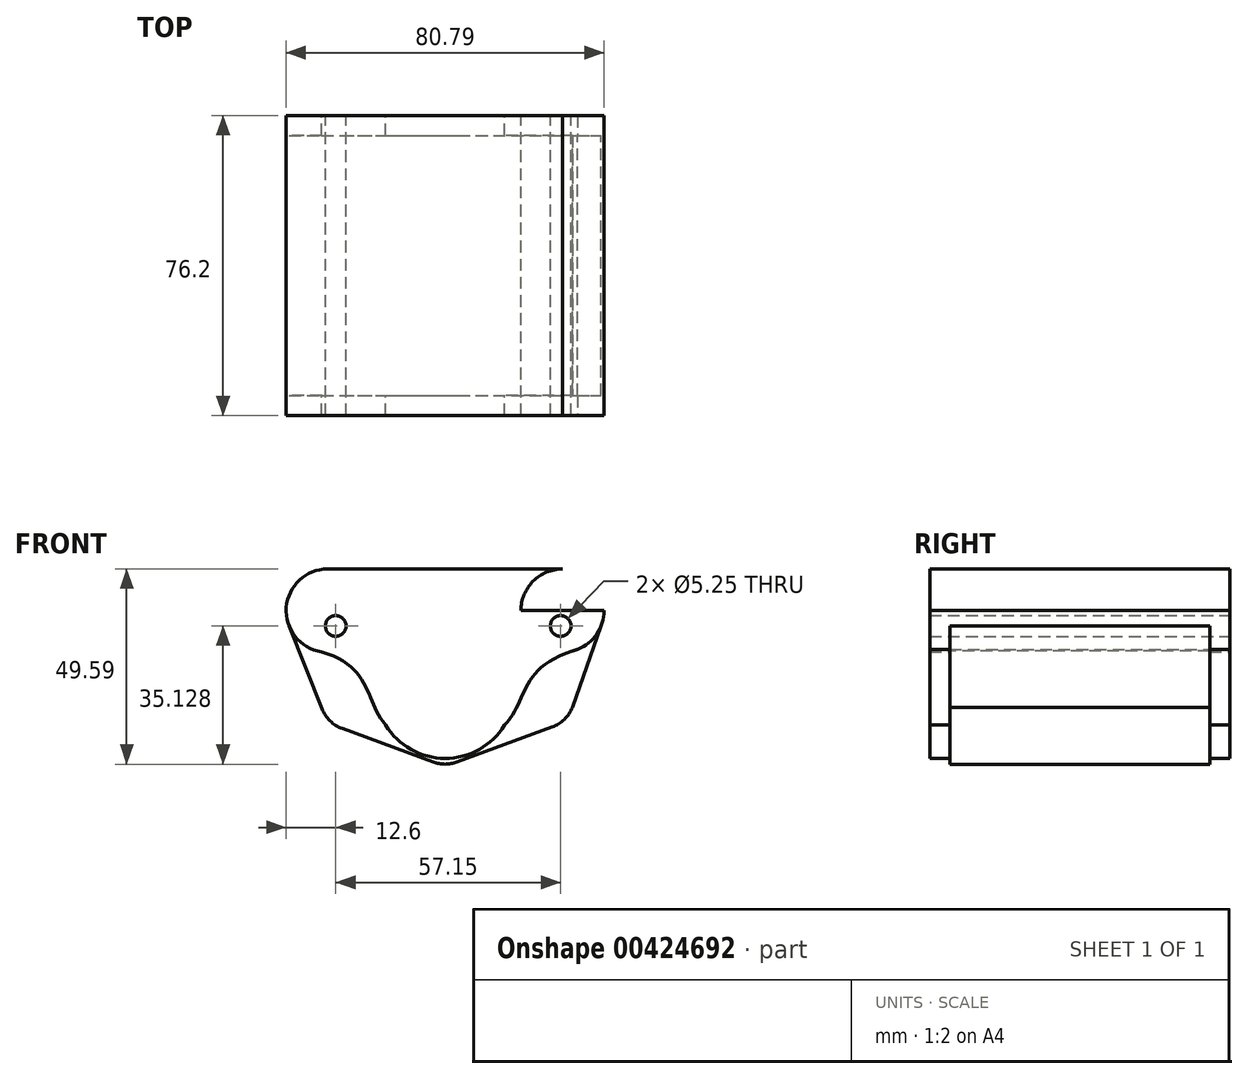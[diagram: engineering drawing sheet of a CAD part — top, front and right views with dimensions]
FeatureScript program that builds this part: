
annotation { "Feature Type Name" : "Feature", "Feature Type Description" : "" }
export const myFeature = defineFeature(function(context is Context, id is Id, definition is map)
    precondition{}
    {
        {
            var Q0;
            Q0=qCreatedBy(makeId("Front.planeOp"),FACE);
            var sketch = newSketch(context, id + "F0", { "sketchPlane" : qUnion([Q0])});
            skLineSegment(sketch, "E0", {"start": v(-40.39, -0.14) * mm, "end": v(40.39, -0.14) * mm});
            skLineSegment(sketch, "E1", {"start": v(0, 11.4) * mm, "end": v(0, -39.74) * mm});
            skCircle(sketch, "E2", {"center": v(0, -20) * mm, "radius": 14.52 * mm});
            skCircle(sketch, "E3", {"center": v(29.82, -0.13) * mm, "radius": 10.56 * mm});
            skCircle(sketch, "E4", {"center": v(-29.83, -0.14) * mm, "radius": 10.56 * mm});
            skLineSegment(sketch, "E5", {"start": v(-29.83, 10.43) * mm, "end": v(29.82, 10.43) * mm});
            skCircle(sketch, "E6", {"center": v(0, -20) * mm, "radius": 17.68 * mm});
            skLineSegment(sketch, "E7", {"start": v(-26.1, -30.13) * mm, "end": v(-3.07, -38.6) * mm});
            skLineSegment(sketch, "E8", {"start": v(3.07, -38.6) * mm, "end": v(27.16, -29.73) * mm});
            skLineSegment(sketch, "E9", {"start": v(32.35, -24.67) * mm, "end": v(39.64, -4.03) * mm});
            skLineSegment(sketch, "E10", {"start": v(-31.3, -25.07) * mm, "end": v(-39.65, -4.04) * mm});
            skArc(sketch, "E11.filletArc", {"start": v(27.16, -29.73) * mm, "mid": v(30.3, -27.76) * mm, "end": v(32.35, -24.67) * mm});
            skPoint(sketch, "E12.visualSharp", {"position": v(-29.83, -28.75) * mm});
            skArc(sketch, "E12.filletArc", {"start": v(-31.3, -25.07) * mm, "mid": v(-29.24, -28.15) * mm, "end": v(-26.1, -30.13) * mm});
            skPoint(sketch, "E13.visualSharp", {"position": v(0, -39.74) * mm});
            skArc(sketch, "E13.filletArc", {"start": v(-3.07, -38.6) * mm, "mid": v(0, -39.16) * mm, "end": v(3.07, -38.6) * mm});
            skPoint(sketch, "E14.1.internal.snap0", {"position": v(15.12, -34.17) * mm});
            skFitSpline(sketch, "E14", {"points": [v(33.66, -9.98) * mm, v(15.12, -29.17) * mm], "startDerivative": vector(-45.98, -13.6) * mm, "endDerivative": vector(-18.55, -19.19) * mm});
            skFitSpline(sketch, "E15", {"points": [v(-31.45, -10.58) * mm, v(-15.12, -29.17) * mm], "startDerivative": vector(39.1, -11.38) * mm, "endDerivative": vector(16.33, -18.6) * mm});
            skCircle(sketch, "E16", {"center": v(29.35, -4.03) * mm, "radius": 2.63 * mm});
            skCircle(sketch, "E17", {"center": v(-27.8, -4.03) * mm, "radius": 2.63 * mm});
            skSolve(sketch);
        }
        {
            var Q0;
            {var subQ0=sQuery(id+"F0.wireOp",EDGE,"E7");Q0=makeQuery(id+"F0.imprint","IMPRINT",FACE,{"disambiguationData":[TD([[makeQuery(id+"F0.imprint","IMPRINT",EDGE,{"derivedFrom":subQ0}),1.0]])]});}
            var Q1;
            {var subQ11=sQuery(id+"F0.wireOp",EDGE,"E8");Q1=makeQuery(id+"F0.imprint","IMPRINT",FACE,{"disambiguationData":[TD([[makeQuery(id+"F0.imprint","IMPRINT",EDGE,{"derivedFrom":subQ11}),1.0]])]});}
            extrude(context, id + "F1", {"entities" : qUnion([Q0, Q1]), "endBound" : BoundingType.SYMMETRIC, "depth" : 66.04 * mm});
        }
        {
            var Q0;
            Q0=makeQuery(id+"F0.imprint","IMPRINT",FACE,{"disambiguationData":[TD([[makeQuery(id+"F0.imprint","IMPRINT",EDGE,{"derivedFrom":sQuery(id+"F0.wireOp",EDGE,"E17")}),-1.0]])]});
            var Q1;
            {var subQ0=sQuery(id+"F0.wireOp",EDGE,"E4");var subQ1=sQuery(id+"F0.wireOp",EDGE,"E0");var subQ2=makeQuery(id+"F0.imprint","INTERSECT",VERTEX,{"derivedFrom":[subQ1,subQ0]});Q1=makeQuery(id+"F0.imprint","IMPRINT",FACE,{"disambiguationData":[TD([[makeQuery(id+"F0.imprint","IMPRINT",EDGE,{"disambiguationData":[TD([[subQ2,-1.0]])],"derivedFrom":subQ1}),1.0]])]});}
            var Q2;
            {var subQ0=sQuery(id+"F0.wireOp",EDGE,"E1");var subQ1=sQuery(id+"F0.wireOp",EDGE,"E0");var subQ2=makeQuery(id+"F0.imprint","INTERSECT",VERTEX,{"derivedFrom":[subQ1,subQ0]});Q2=makeQuery(id+"F0.imprint","IMPRINT",FACE,{"disambiguationData":[TD([[makeQuery(id+"F0.imprint","IMPRINT",EDGE,{"disambiguationData":[TD([[subQ2,-1.0]])],"derivedFrom":subQ1}),1.0]])]});}
            var Q3;
            {var subQ0=sQuery(id+"F0.wireOp",EDGE,"E3");var subQ1=sQuery(id+"F0.wireOp",EDGE,"E0");var subQ2=makeQuery(id+"F0.imprint","INTERSECT",VERTEX,{"disambiguationData":[OD(0.0)],"derivedFrom":[subQ1,subQ0]});Q3=makeQuery(id+"F0.imprint","IMPRINT",FACE,{"disambiguationData":[TD([[makeQuery(id+"F0.imprint","IMPRINT",EDGE,{"disambiguationData":[TD([[subQ2,1.0]])],"derivedFrom":subQ1}),1.0]])]});}
            var Q4;
            Q4=makeQuery(id+"F0.imprint","IMPRINT",FACE,{"disambiguationData":[TD([[makeQuery(id+"F0.imprint","IMPRINT",EDGE,{"derivedFrom":sQuery(id+"F0.wireOp",EDGE,"E16")}),-1.0]])]});
            var Q5;
            {var subQ1=sQuery(id+"F0.wireOp",EDGE,"E0");var subQ5=sQuery(id+"F0.wireOp",EDGE,"E1");var subQ6=makeQuery(id+"F0.imprint","INTERSECT",VERTEX,{"derivedFrom":[subQ1,subQ5]});Q5=makeQuery(id+"F0.imprint","IMPRINT",FACE,{"disambiguationData":[TD([[makeQuery(id+"F0.imprint","IMPRINT",EDGE,{"disambiguationData":[TD([[subQ6,-1.0]])],"derivedFrom":subQ1}),-1.0]])]});}
            var Q6;
            {var subQ1=sQuery(id+"F0.wireOp",EDGE,"E1");var subQ3=sQuery(id+"F0.wireOp",EDGE,"E6");var subQ7=makeQuery(id+"F0.imprint","INTERSECT",VERTEX,{"disambiguationData":[OD(0.0)],"derivedFrom":[subQ1,subQ3]});Q6=makeQuery(id+"F0.imprint","IMPRINT",FACE,{"disambiguationData":[TD([[makeQuery(id+"F0.imprint","IMPRINT",EDGE,{"disambiguationData":[TD([[subQ7,-1.0]])],"derivedFrom":subQ1}),1.0]])]});}
            var Q7;
            {var subQ0=sQuery(id+"F0.wireOp",EDGE,"E15");Q7=makeQuery(id+"F0.imprint","IMPRINT",FACE,{"disambiguationData":[TD([[makeQuery(id+"F0.imprint","IMPRINT",EDGE,{"derivedFrom":subQ0}),1.0]])]});}
            var Q8;
            {var subQ0=sQuery(id+"F0.wireOp",EDGE,"E6");var subQ2=sQuery(id+"F0.wireOp",EDGE,"E1");var subQ3=makeQuery(id+"F0.imprint","INTERSECT",VERTEX,{"disambiguationData":[OD(0.0)],"derivedFrom":[subQ2,subQ0]});Q8=makeQuery(id+"F0.imprint","IMPRINT",FACE,{"disambiguationData":[TD([[makeQuery(id+"F0.imprint","IMPRINT",EDGE,{"disambiguationData":[TD([[subQ3,-1.0]])],"derivedFrom":subQ2}),-1.0]])]});}
            var Q9;
            {var subQ0=sQuery(id+"F0.wireOp",EDGE,"E2");var subQ1=sQuery(id+"F0.wireOp",EDGE,"E1");var subQ2=makeQuery(id+"F0.imprint","INTERSECT",VERTEX,{"disambiguationData":[OD(0.0)],"derivedFrom":[subQ1,subQ0]});Q9=makeQuery(id+"F0.imprint","IMPRINT",FACE,{"disambiguationData":[TD([[makeQuery(id+"F0.imprint","IMPRINT",EDGE,{"disambiguationData":[TD([[subQ2,-1.0]])],"derivedFrom":subQ1}),-1.0]])]});}
            var Q10;
            {var subQ0=sQuery(id+"F0.wireOp",EDGE,"E2");var subQ1=sQuery(id+"F0.wireOp",EDGE,"E1");var subQ2=makeQuery(id+"F0.imprint","INTERSECT",VERTEX,{"disambiguationData":[OD(0.0)],"derivedFrom":[subQ1,subQ0]});Q10=makeQuery(id+"F0.imprint","IMPRINT",FACE,{"disambiguationData":[TD([[makeQuery(id+"F0.imprint","IMPRINT",EDGE,{"disambiguationData":[TD([[subQ2,-1.0]])],"derivedFrom":subQ1}),1.0]])]});}
            extrude(context, id + "F2", {"entities" : qUnion([Q0, Q1, Q2, Q3, Q4, Q5, Q6, Q7, Q8, Q9, Q10]), "operationType" : NewBodyOperationType.ADD, "endBound" : BoundingType.SYMMETRIC, "depth" : 76.2 * mm});
        }
    });
